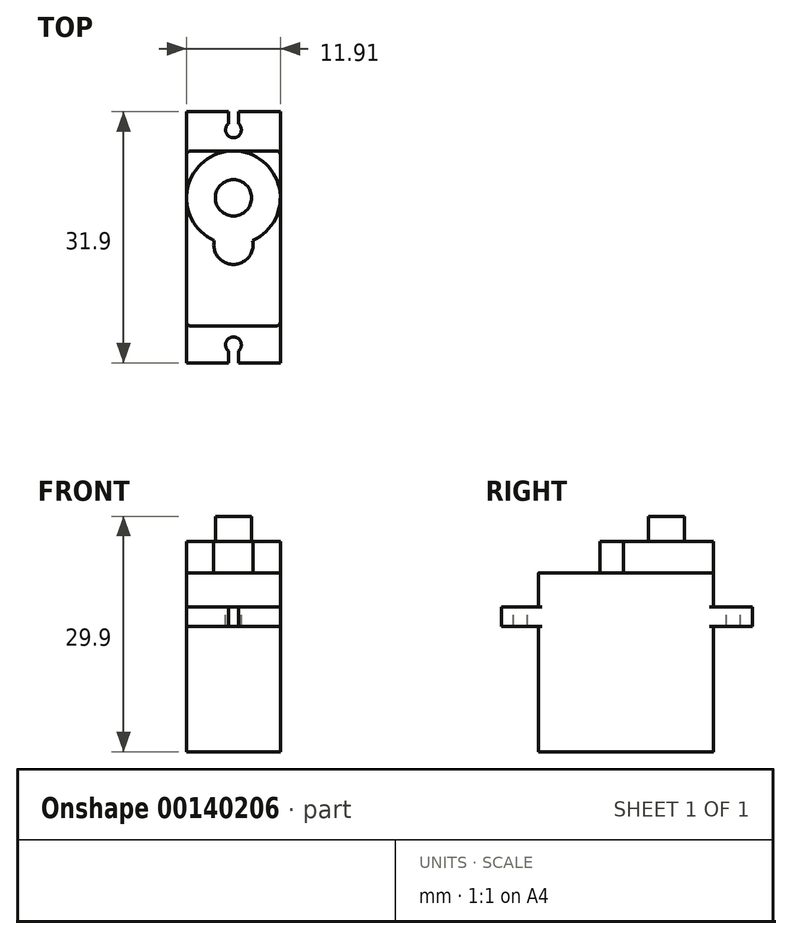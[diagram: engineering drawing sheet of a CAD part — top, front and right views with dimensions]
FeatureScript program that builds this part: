
annotation { "Feature Type Name" : "Feature", "Feature Type Description" : "" }
export const myFeature = defineFeature(function(context is Context, id is Id, definition is map)
    precondition{}
    {
        {
            var Q0;
            Q0=qCreatedBy(makeId("Top.planeOp"),FACE);
            var sketch = newSketch(context, id + "F0", { "sketchPlane" : qUnion([Q0])});
            skLineSegment(sketch, "E0", {"start": v(0, 0.5) * mm, "end": v(0, 21.73) * mm});
            skLineSegment(sketch, "E1", {"start": v(0.5, 22.23) * mm, "end": v(11.4, 22.23) * mm});
            skLineSegment(sketch, "E2", {"start": v(11.9, 21.73) * mm, "end": v(11.9, 0.5) * mm});
            skLineSegment(sketch, "E3", {"start": v(11.4, 0) * mm, "end": v(0.5, 0) * mm});
            skPoint(sketch, "E4.visualSharp", {"position": v(0, 22.23) * mm});
            skArc(sketch, "E4.filletArc", {"start": v(0.5, 22.23) * mm, "mid": v(0.15, 22.08) * mm, "end": v(0, 21.73) * mm});
            skPoint(sketch, "E5.visualSharp", {"position": v(11.9, 22.23) * mm});
            skArc(sketch, "E5.filletArc", {"start": v(11.9, 21.73) * mm, "mid": v(11.76, 22.08) * mm, "end": v(11.4, 22.23) * mm});
            skPoint(sketch, "E6.visualSharp", {"position": v(11.9, 0) * mm});
            skArc(sketch, "E6.filletArc", {"start": v(11.4, 0) * mm, "mid": v(11.76, 0.15) * mm, "end": v(11.9, 0.5) * mm});
            skPoint(sketch, "E7.visualSharp", {"position": v(0, 0) * mm});
            skArc(sketch, "E7.filletArc", {"start": v(0, 0.5) * mm, "mid": v(0.15, 0.15) * mm, "end": v(0.5, 0) * mm});
            skSolve(sketch);
        }
        {
            var Q0;
            Q0=makeQuery(id+"F0.imprint","IMPRINT",FACE,{"disambiguationData":[TD([[makeQuery(id+"F0.imprint","IMPRINT",EDGE,{"derivedFrom":sQuery(id+"F0.wireOp",EDGE,"E0")}),-1.0]])]});
            extrude(context, id + "F1", {"entities" : qUnion([Q0]), "depth" : 16 * mm});
        }
        {
            var Q0;
            Q0=makeQuery(id+"F1.opExtrude","CAP_FACE",FACE,{"disambiguationData":[OSD([sQuery(id+"F0.wireOp",EDGE,"E0"),sQuery(id+"F0.wireOp",EDGE,"E1"),sQuery(id+"F0.wireOp",EDGE,"E2"),sQuery(id+"F0.wireOp",EDGE,"E3"),sQuery(id+"F0.wireOp",EDGE,"E4.filletArc"),sQuery(id+"F0.wireOp",EDGE,"E5.filletArc"),sQuery(id+"F0.wireOp",EDGE,"E6.filletArc"),sQuery(id+"F0.wireOp",EDGE,"E7.filletArc")])],"isStart":false});
            extrude(context, id + "F2", {"entities" : qUnion([Q0]), "operationType" : NewBodyOperationType.ADD, "depth" : 6.7 * mm});
        }
        {
            var Q0;
            Q0=makeQuery(id+"F2.opExtrude","CAP_FACE",FACE,{"disambiguationData":[OSD([sQuery(id+"F0.wireOp",EDGE,"E0"),sQuery(id+"F0.wireOp",EDGE,"E1"),sQuery(id+"F0.wireOp",EDGE,"E2"),sQuery(id+"F0.wireOp",EDGE,"E3"),sQuery(id+"F0.wireOp",EDGE,"E4.filletArc"),sQuery(id+"F0.wireOp",EDGE,"E5.filletArc"),sQuery(id+"F0.wireOp",EDGE,"E6.filletArc"),sQuery(id+"F0.wireOp",EDGE,"E7.filletArc")])],"isStart":false});
            var sketch = newSketch(context, id + "F3", { "sketchPlane" : qUnion([Q0])});
            skLineSegment(sketch, "E8", {"start": v(0, 16.27) * mm, "end": v(11.9, 16.27) * mm, "construction": true});
            skArc(sketch, "E9", {"start": v(8.4, 10.84) * mm, "mid": v(5.95, 22.23) * mm, "end": v(3.5, 10.84) * mm});
            skLineSegment(sketch, "E10", {"start": v(5.95, 16.27) * mm, "end": v(5.95, 5.27) * mm, "construction": true});
            skArc(sketch, "E11", {"start": v(3.5, 10.84) * mm, "mid": v(5.95, 7.82) * mm, "end": v(8.4, 10.84) * mm});
            skSolve(sketch);
        }
        {
            var Q0;
            {var subQ0=sQuery(id+"F3.wireOp",EDGE,"E11");Q0=makeQuery(id+"F3.imprint","IMPRINT",FACE,{"disambiguationData":[TD([[makeQuery(id+"F3.imprint","IMPRINT",EDGE,{"derivedFrom":subQ0}),1.0]])]});}
            extrude(context, id + "F4", {"entities" : qUnion([Q0]), "operationType" : NewBodyOperationType.ADD, "depth" : 4 * mm});
        }
        {
            var Q0;
            Q0=makeQuery(id+"F4.opExtrude","CAP_FACE",FACE,{"disambiguationData":[OSD([sQuery(id+"F3.wireOp",EDGE,"E9"),sQuery(id+"F3.wireOp",EDGE,"E11")])],"isStart":false});
            var sketch = newSketch(context, id + "F5", { "sketchPlane" : qUnion([Q0])});
            skLineSegment(sketch, "E12", {"start": v(5.95, 22.23) * mm, "end": v(5.95, 7.82) * mm, "construction": true});
            skLineSegment(sketch, "E13", {"start": v(0, 16.27) * mm, "end": v(11.9, 16.27) * mm, "construction": true});
            skCircle(sketch, "E14", {"center": v(5.95, 16.27) * mm, "radius": 2.3 * mm});
            skSolve(sketch);
        }
        {
            var Q0;
            Q0=makeQuery(id+"F5.imprint","IMPRINT",FACE,{"disambiguationData":[TD([[makeQuery(id+"F5.imprint","IMPRINT",EDGE,{"derivedFrom":sQuery(id+"F5.wireOp",EDGE,"E14")}),1.0]])]});
            extrude(context, id + "F6", {"entities" : qUnion([Q0]), "operationType" : NewBodyOperationType.ADD, "depth" : 3.2 * mm});
        }
        {
            var Q0;
            {var subQ0=sQuery(id+"F0.wireOp",EDGE,"E3");Q0=makeQuery(id+"F2.boolean.opBoolean","MERGE",FACE,{"derivedFrom":[makeQuery(id+"F1.opExtrude","SWEPT_FACE",FACE,{"disambiguationData":[OSD([subQ0])]}),makeQuery(id+"F2.opExtrude","SWEPT_FACE",FACE,{"disambiguationData":[OSD([subQ0])]})]});}
            var sketch = newSketch(context, id + "F7", { "sketchPlane" : qUnion([Q0])});
            skLineSegment(sketch, "E15", {"start": v(5.95, 22.7) * mm, "end": v(5.95, 0) * mm, "construction": true});
            skLineSegment(sketch, "E16", {"start": v(0.5, 18.4) * mm, "end": v(11.4, 18.4) * mm, "construction": true});
            skLineSegment(sketch, "E17", {"start": v(0, 18.4) * mm, "end": v(11.9, 18.4) * mm});
            skLineSegment(sketch, "E18", {"start": v(11.9, 18.4) * mm, "end": v(11.9, 15.9) * mm});
            skLineSegment(sketch, "E19", {"start": v(11.9, 15.9) * mm, "end": v(0, 15.9) * mm});
            skLineSegment(sketch, "E20", {"start": v(0, 15.9) * mm, "end": v(0, 18.4) * mm});
            skSolve(sketch);
        }
        {
            var Q0;
            {var subQ7=sQuery(id+"F7.wireOp",EDGE,"E18");Q0=makeQuery(id+"F7.imprint","IMPRINT",FACE,{"disambiguationData":[TD([[makeQuery(id+"F7.imprint","IMPRINT",EDGE,{"derivedFrom":subQ7}),-1.0]])]});}
            var Q1;
            {var subQ0=sQuery(id+"F0.wireOp",EDGE,"E3");var subQ1=sQuery(id+"F0.wireOp",EDGE,"E7.filletArc");var subQ2=makeQuery(id+"F2.boolean.opBoolean","MERGE",EDGE,{"derivedFrom":[makeQuery(id+"F1.opExtrude","SWEPT_EDGE",EDGE,{"disambiguationData":[OSD([subQ0,subQ1])]}),makeQuery(id+"F2.opExtrude","SWEPT_EDGE",EDGE,{"disambiguationData":[OSD([subQ0,subQ1])]})]});var subQ5=sQuery(id+"F7.wireOp",EDGE,"E17");var subQ6=makeQuery(id+"F7.imprint","INTERSECT",VERTEX,{"derivedFrom":[subQ2,subQ5]});Q1=makeQuery(id+"F7.imprint","IMPRINT",FACE,{"disambiguationData":[TD([[makeQuery(id+"F7.imprint","IMPRINT",EDGE,{"disambiguationData":[TD([[subQ6,-1.0]])],"derivedFrom":subQ5}),-1.0]])]});}
            var Q2;
            {var subQ7=sQuery(id+"F7.wireOp",EDGE,"E20");Q2=makeQuery(id+"F7.imprint","IMPRINT",FACE,{"disambiguationData":[TD([[makeQuery(id+"F7.imprint","IMPRINT",EDGE,{"derivedFrom":subQ7}),-1.0]])]});}
            extrude(context, id + "F8", {"entities" : qUnion([Q0, Q1, Q2]), "operationType" : NewBodyOperationType.ADD, "oppositeDirection" : true, "depth" : 1 * mm});
        }
        {
            var Q0;
            {var subQ0=sQuery(id+"F0.wireOp",EDGE,"E3");Q0=makeQuery(id+"F8.boolean.opBoolean","MERGE",FACE,{"derivedFrom":[makeQuery(id+"F2.boolean.opBoolean","MERGE",FACE,{"derivedFrom":[makeQuery(id+"F1.opExtrude","SWEPT_FACE",FACE,{"disambiguationData":[OSD([subQ0])]}),makeQuery(id+"F2.opExtrude","SWEPT_FACE",FACE,{"disambiguationData":[OSD([subQ0])]})]}),makeQuery(id+"F8.opExtrude","CAP_FACE",FACE,{"disambiguationData":[OSD([sQuery(id+"F7.wireOp",EDGE,"E17"),sQuery(id+"F7.wireOp",EDGE,"E18"),sQuery(id+"F7.wireOp",EDGE,"E19"),sQuery(id+"F7.wireOp",EDGE,"E20")])],"isStart":true})]});}
            var sketch = newSketch(context, id + "F9", { "sketchPlane" : qUnion([Q0])});
            skLineSegment(sketch, "E21", {"start": v(0.5, 18.4) * mm, "end": v(11.4, 18.4) * mm});
            skLineSegment(sketch, "E22", {"start": v(0.5, 15.9) * mm, "end": v(11.4, 15.9) * mm});
            skSolve(sketch);
        }
        {
            var Q0;
            Q0=makeQuery(id+"F9.imprint","IMPRINT",FACE,{"disambiguationData":[TD([[makeQuery(id+"F9.imprint","IMPRINT",EDGE,{"derivedFrom":sQuery(id+"F9.wireOp",EDGE,"E21")}),-1.0]])]});
            extrude(context, id + "F10", {"entities" : qUnion([Q0]), "operationType" : NewBodyOperationType.ADD, "depth" : 4.7 * mm});
        }
        {
            var Q0;
            Q0=makeQuery(id+"F10.opExtrude","CAP_FACE",FACE,{"disambiguationData":[OSD([sQuery(id+"F7.wireOp",EDGE,"E17"),sQuery(id+"F7.wireOp",EDGE,"E18"),sQuery(id+"F7.wireOp",EDGE,"E19"),sQuery(id+"F7.wireOp",EDGE,"E20"),sQuery(id+"F9.wireOp",EDGE,"E21"),sQuery(id+"F9.wireOp",EDGE,"E22")])],"isStart":false});
            extrude(context, id + "F11", {"entities" : qUnion([Q0]), "operationType" : NewBodyOperationType.ADD, "oppositeDirection" : true, "depth" : 31.9 * mm});
        }
        {
            var Q0;
            {var subQ0=sQuery(id+"F7.wireOp",EDGE,"E17");var subQ1=makeQuery(id+"F8.opExtrude","SWEPT_FACE",FACE,{"disambiguationData":[OSD([subQ0])]});var subQ8=sQuery(id+"F0.wireOp",EDGE,"E0");var subQ10=sQuery(id+"F0.wireOp",EDGE,"E2");Q0=makeQuery(id+"F10.boolean.opBoolean","MERGE",FACE,{"derivedFrom":[makeQuery(id+"F8.boolean.opBoolean","SPLIT",FACE,{"disambiguationData":[TD([makeQuery(id+"F1.opExtrude","SWEPT_FACE",FACE,{"disambiguationData":[OSD([subQ8])]})])],"derivedFrom":subQ1}),makeQuery(id+"F8.boolean.opBoolean","SPLIT",FACE,{"disambiguationData":[TD([makeQuery(id+"F1.opExtrude","SWEPT_FACE",FACE,{"disambiguationData":[OSD([subQ10])]})])],"derivedFrom":subQ1}),makeQuery(id+"F10.opExtrude","SWEPT_FACE",FACE,{"disambiguationData":[OSD([subQ0,sQuery(id+"F9.wireOp",EDGE,"E21")])]})]});}
            var sketch = newSketch(context, id + "F12", { "sketchPlane" : qUnion([Q0])});
            skLineSegment(sketch, "E23", {"start": v(0, -2.4) * mm, "end": v(11.9, -2.4) * mm, "construction": true});
            skArc(sketch, "E24", {"start": v(6.6, -3.16) * mm, "mid": v(5.95, -1.4) * mm, "end": v(5.3, -3.16) * mm});
            skLineSegment(sketch, "E25", {"start": v(5.95, -2.4) * mm, "end": v(5.95, -4.7) * mm, "construction": true});
            skLineSegment(sketch, "E26", {"start": v(6.6, -4.7) * mm, "end": v(6.6, -3.16) * mm});
            skLineSegment(sketch, "E27", {"start": v(5.3, -4.7) * mm, "end": v(5.3, -3.16) * mm});
            skSolve(sketch);
        }
        {
            var Q0;
            Q0=makeQuery(id+"F12.imprint","IMPRINT",FACE,{"disambiguationData":[TD([[makeQuery(id+"F12.imprint","IMPRINT",EDGE,{"derivedFrom":sQuery(id+"F12.wireOp",EDGE,"E24")}),1.0]])]});
            extrude(context, id + "F13", {"entities" : qUnion([Q0]), "operationType" : NewBodyOperationType.REMOVE, "endBound" : BoundingType.UP_TO_NEXT, "oppositeDirection" : true, "depth" : 25.4 * mm});
        }
        {
            var Q0;
            Q0=makeQuery(id+"F11.opExtrude","SWEPT_FACE",FACE,{"disambiguationData":[OSD([sQuery(id+"F7.wireOp",EDGE,"E17"),sQuery(id+"F9.wireOp",EDGE,"E21")])]});
            var sketch = newSketch(context, id + "F14", { "sketchPlane" : qUnion([Q0])});
            skLineSegment(sketch, "E28", {"start": v(0, 24.9) * mm, "end": v(11.9, 24.9) * mm, "construction": true});
            skArc(sketch, "E29", {"start": v(5.3, 25.66) * mm, "mid": v(5.95, 23.9) * mm, "end": v(6.6, 25.66) * mm});
            skLineSegment(sketch, "E30", {"start": v(5.95, 24.9) * mm, "end": v(5.95, 27.2) * mm, "construction": true});
            skLineSegment(sketch, "E31", {"start": v(5.3, 27.2) * mm, "end": v(5.3, 25.66) * mm});
            skLineSegment(sketch, "E32", {"start": v(6.6, 27.2) * mm, "end": v(6.6, 25.66) * mm});
            skSolve(sketch);
        }
        {
            var Q0;
            Q0=makeQuery(id+"F14.imprint","IMPRINT",FACE,{"disambiguationData":[TD([[makeQuery(id+"F14.imprint","IMPRINT",EDGE,{"derivedFrom":sQuery(id+"F14.wireOp",EDGE,"E29")}),1.0]])]});
            extrude(context, id + "F15", {"entities" : qUnion([Q0]), "operationType" : NewBodyOperationType.REMOVE, "endBound" : BoundingType.UP_TO_NEXT, "oppositeDirection" : true, "depth" : 25.4 * mm});
        }
        {
            var Q0;
            Q0=makeQuery(id+"F1.opExtrude","SWEPT_BODY",BODY,{"disambiguationData":[OSD([sQuery(id+"F0.wireOp",EDGE,"E0"),sQuery(id+"F0.wireOp",EDGE,"E1"),sQuery(id+"F0.wireOp",EDGE,"E2"),sQuery(id+"F0.wireOp",EDGE,"E3"),sQuery(id+"F0.wireOp",EDGE,"E4.filletArc"),sQuery(id+"F0.wireOp",EDGE,"E5.filletArc"),sQuery(id+"F0.wireOp",EDGE,"E6.filletArc"),sQuery(id+"F0.wireOp",EDGE,"E7.filletArc")])]});
            transform(context, id + "F16", {"entities" : qUnion([Q0]), "transformType" : TransformType.TRANSLATION_3D, "dx" : 0 * mm, "dy" : 0 * mm, "dz" : 0 * mm, "makeCopy" : true});
        }
        {
            var Q0;
            Q0=makeQuery(id+"F16.opPattern","COPY",BODY,{"derivedFrom":makeQuery(id+"F1.opExtrude","SWEPT_BODY",BODY,{"disambiguationData":[OSD([sQuery(id+"F0.wireOp",EDGE,"E0"),sQuery(id+"F0.wireOp",EDGE,"E1"),sQuery(id+"F0.wireOp",EDGE,"E2"),sQuery(id+"F0.wireOp",EDGE,"E3"),sQuery(id+"F0.wireOp",EDGE,"E4.filletArc"),sQuery(id+"F0.wireOp",EDGE,"E5.filletArc"),sQuery(id+"F0.wireOp",EDGE,"E6.filletArc"),sQuery(id+"F0.wireOp",EDGE,"E7.filletArc")])]}),"instanceName":"1"});
            deleteBodies(context, id + "F17", {"entities" : qUnion([Q0])});
        }
        {
            var Q0;
            Q0=makeQuery(id+"F1.opExtrude","SWEPT_BODY",BODY,{"disambiguationData":[OSD([sQuery(id+"F0.wireOp",EDGE,"E0"),sQuery(id+"F0.wireOp",EDGE,"E1"),sQuery(id+"F0.wireOp",EDGE,"E2"),sQuery(id+"F0.wireOp",EDGE,"E3"),sQuery(id+"F0.wireOp",EDGE,"E4.filletArc"),sQuery(id+"F0.wireOp",EDGE,"E5.filletArc"),sQuery(id+"F0.wireOp",EDGE,"E6.filletArc"),sQuery(id+"F0.wireOp",EDGE,"E7.filletArc")])]});
            transform(context, id + "F18", {"entities" : qUnion([Q0]), "transformType" : TransformType.TRANSLATION_3D, "dx" : 0 * mm, "dy" : 0 * mm, "dz" : 0 * mm, "makeCopy" : true});
        }
    });
